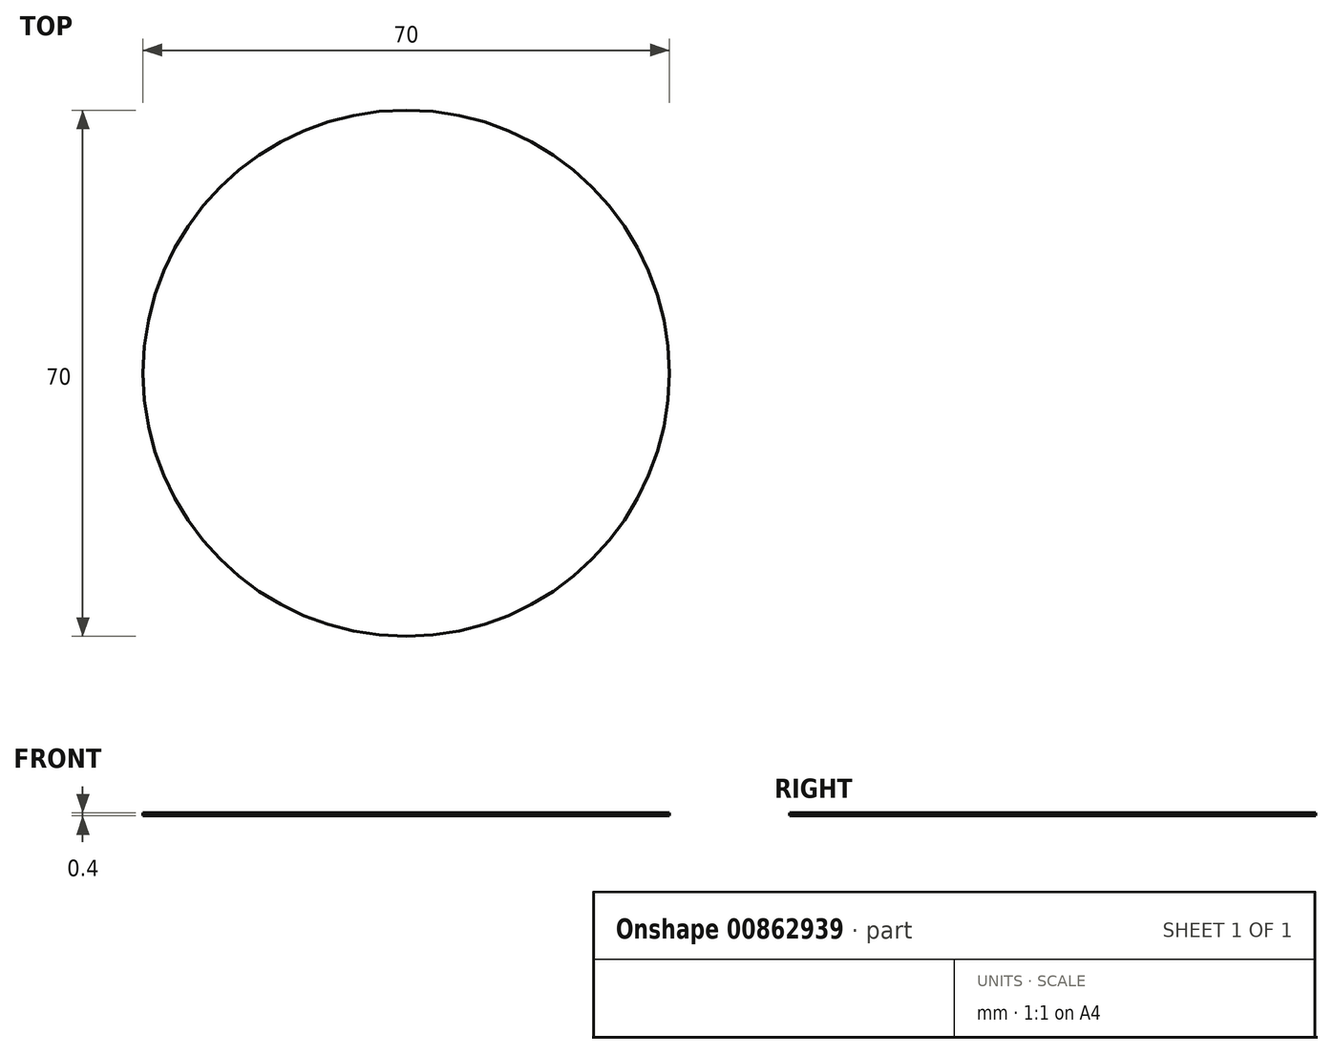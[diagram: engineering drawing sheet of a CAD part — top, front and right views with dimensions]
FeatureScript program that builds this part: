
annotation { "Feature Type Name" : "Feature", "Feature Type Description" : "" }
export const myFeature = defineFeature(function(context is Context, id is Id, definition is map)
    precondition{}
    {
        {
            var Q0;
            Q0=qCreatedBy(makeId("Top.planeOp"),FACE);
            var sketch = newSketch(context, id + "F0", { "sketchPlane" : qUnion([Q0])});
            skCircle(sketch, "E0", {"center": v(0, 0) * mm, "radius": 35 * mm});
            skSolve(sketch);
        }
        {
            var Q0;
            Q0=makeQuery(id+"F0.imprint","IMPRINT",FACE,{"disambiguationData":[TD([[makeQuery(id+"F0.imprint","IMPRINT",EDGE,{"derivedFrom":sQuery(id+"F0.wireOp",EDGE,"E0")}),1.0]])]});
            extrude(context, id + "F1", {"entities" : qUnion([Q0]), "depth" : 0.4 * mm, "offsetDistance" : 25 * mm});
        }
    });
